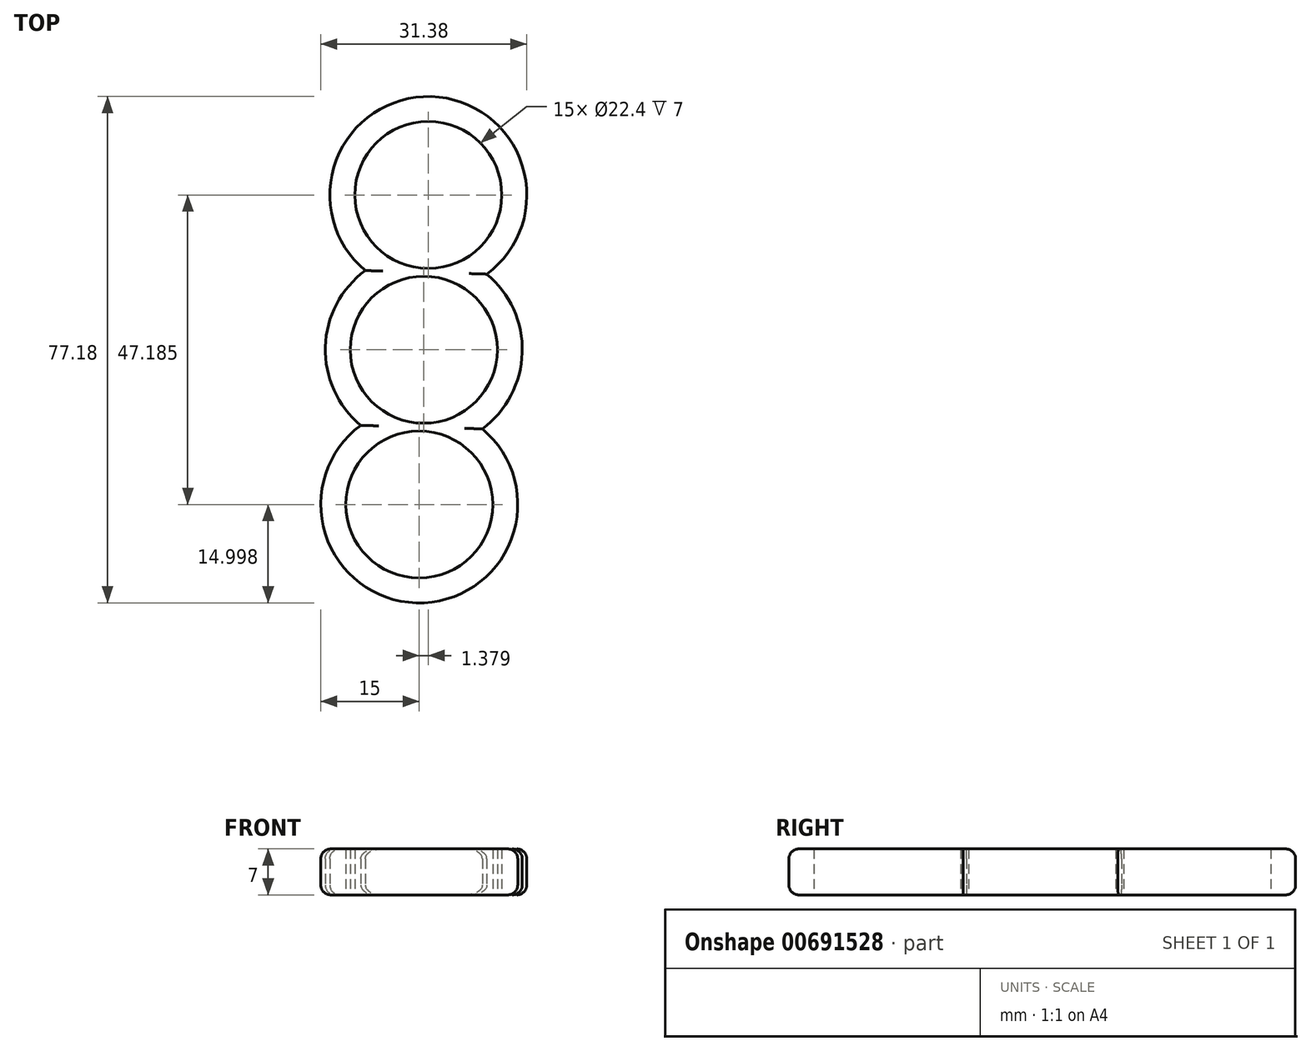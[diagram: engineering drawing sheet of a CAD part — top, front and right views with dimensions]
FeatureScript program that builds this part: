
annotation { "Feature Type Name" : "Feature", "Feature Type Description" : "" }
export const myFeature = defineFeature(function(context is Context, id is Id, definition is map)
    precondition{}
    {
        {
            var Q0;
            Q0=qCreatedBy(makeId("Top.planeOp"),FACE);
            var sketch = newSketch(context, id + "F0", { "sketchPlane" : qUnion([Q0])});
            skCircle(sketch, "E0", {"center": v(0, 0) * mm, "radius": 11.2 * mm});
            skCircle(sketch, "E1.1.0", {"center": v(-0.69, -23.6) * mm, "radius": 11.2 * mm});
            skPoint(sketch, "E1.center", {"position": v(-0.34, 1.61) * mm});
            skCircle(sketch, "E2.1.0", {"center": v(0.69, 23.6) * mm, "radius": 11.2 * mm});
            skCircle(sketch, "E3", {"center": v(-0.69, -23.6) * mm, "radius": 15 * mm});
            skCircle(sketch, "E4", {"center": v(0, 0) * mm, "radius": 15 * mm});
            skCircle(sketch, "E5", {"center": v(0.69, 23.6) * mm, "radius": 15 * mm});
            skSolve(sketch);
        }
        {
            var Q0;
            Q0=qSketchRegion(id+"F0",true);
            extrude(context, id + "F1", {"entities" : qUnion([Q0]), "depth" : 7 * mm, "offsetDistance" : 25 * mm});
        }
        {
            var Q0;
            Q0=makeQuery(id+"F1.opExtrude","CAP_EDGE",EDGE,{"disambiguationData":[OSD([sQuery(id+"F0.wireOp",EDGE,"KVhzaLa0-SQdz-q6Oe-w92h-Agfz15YDrdAH")])],"isStart":false});
            var Q1;
            Q1=makeQuery(id+"F1.opExtrude","CAP_EDGE",EDGE,{"disambiguationData":[OSD([sQuery(id+"F0.wireOp",EDGE,"ff2df07f-f202-44d3-8f0e-1026d9d6524d.2.1")])],"isStart":false});
            var Q2;
            Q2=makeQuery(id+"F1.opExtrude","CAP_EDGE",EDGE,{"disambiguationData":[OSD([sQuery(id+"F0.wireOp",EDGE,"ff2df07f-f202-44d3-8f0e-1026d9d6524d.1.1")])],"isStart":false});
            var Q3;
            Q3=makeQuery(id+"F1.opExtrude","CAP_EDGE",EDGE,{"disambiguationData":[OSD([sQuery(id+"F0.wireOp",EDGE,"E3TO4OPZ-r4YO-zi4T-4Kzq-n9bXmHvUswec")])],"isStart":false});
            var Q4;
            Q4=makeQuery(id+"F1.opExtrude","CAP_EDGE",EDGE,{"disambiguationData":[OSD([sQuery(id+"F0.wireOp",EDGE,"ff2df07f-f202-44d3-8f0e-1026d9d6524d.2.1")])],"isStart":true});
            var Q5;
            Q5=makeQuery(id+"F1.opExtrude","CAP_EDGE",EDGE,{"disambiguationData":[OSD([sQuery(id+"F0.wireOp",EDGE,"b95ef4d3-2bef-4a45-8702-1981668bb12b.1.0")])],"isStart":true});
            var Q6;
            Q6=makeQuery(id+"F1.opExtrude","CAP_EDGE",EDGE,{"disambiguationData":[OSD([sQuery(id+"F0.wireOp",EDGE,"E3TO4OPZ-r4YO-zi4T-4Kzq-n9bXmHvUswec")])],"isStart":true});
            var Q7;
            Q7=makeQuery(id+"F1.opExtrude","CAP_EDGE",EDGE,{"disambiguationData":[OSD([sQuery(id+"F0.wireOp",EDGE,"ff2df07f-f202-44d3-8f0e-1026d9d6524d.1.1")])],"isStart":true});
            var Q8;
            Q8=makeQuery(id+"F1.opExtrude","CAP_EDGE",EDGE,{"disambiguationData":[OSD([sQuery(id+"F0.wireOp",EDGE,"HvMq5l3T-N398-ElJL-TXP7-qc9evoMqA3Qe")])],"isStart":false});
            var Q9;
            Q9=makeQuery(id+"F1.opExtrude","CAP_EDGE",EDGE,{"disambiguationData":[OSD([sQuery(id+"F0.wireOp",EDGE,"6a3b17aa-de62-40af-a578-fda0c71b9185")])],"isStart":false});
            var Q10;
            Q10=makeQuery(id+"F1.opExtrude","CAP_EDGE",EDGE,{"disambiguationData":[OSD([sQuery(id+"F0.wireOp",EDGE,"HvMq5l3T-N398-ElJL-TXP7-qc9evoMqA3Qe")])],"isStart":true});
            var Q11;
            Q11=makeQuery(id+"F1.opExtrude","CAP_EDGE",EDGE,{"disambiguationData":[OSD([sQuery(id+"F0.wireOp",EDGE,"6a3b17aa-de62-40af-a578-fda0c71b9185")])],"isStart":true});
            var Q12;
            {var subQ0=sQuery(id+"F0.wireOp",EDGE,"e1ec5250-1445-4ff0-901a-2fadd4f62a60");Q12=makeQuery(id+"F1.opExtrude","CAP_EDGE",EDGE,{"disambiguationData":[OSD([subQ0]),TDD([makeQuery(id+"F0.imprint","IMPRINT",EDGE,{"disambiguationData":[TD([[makeQuery(id+"F0.imprint","INTERSECT",VERTEX,{"disambiguationData":[OD(0.0)],"derivedFrom":[sQuery(id+"F0.wireOp",EDGE,"HvMq5l3T-N398-ElJL-TXP7-qc9evoMqA3Qe"),subQ0]}),-1.0]])],"derivedFrom":subQ0})])],"isStart":false});}
            var Q13;
            {var subQ0=sQuery(id+"F0.wireOp",EDGE,"e1ec5250-1445-4ff0-901a-2fadd4f62a60");Q13=makeQuery(id+"F1.opExtrude","CAP_EDGE",EDGE,{"disambiguationData":[OSD([subQ0]),TDD([makeQuery(id+"F0.imprint","IMPRINT",EDGE,{"disambiguationData":[TD([[makeQuery(id+"F0.imprint","INTERSECT",VERTEX,{"disambiguationData":[OD(1.0)],"derivedFrom":[sQuery(id+"F0.wireOp",EDGE,"HvMq5l3T-N398-ElJL-TXP7-qc9evoMqA3Qe"),subQ0]}),1.0]])],"derivedFrom":subQ0})])],"isStart":false});}
            var Q14;
            {var subQ0=sQuery(id+"F0.wireOp",EDGE,"e1ec5250-1445-4ff0-901a-2fadd4f62a60");Q14=makeQuery(id+"F1.opExtrude","CAP_EDGE",EDGE,{"disambiguationData":[OSD([subQ0]),TDD([makeQuery(id+"F0.imprint","IMPRINT",EDGE,{"disambiguationData":[TD([[makeQuery(id+"F0.imprint","INTERSECT",VERTEX,{"disambiguationData":[OD(0.0)],"derivedFrom":[sQuery(id+"F0.wireOp",EDGE,"HvMq5l3T-N398-ElJL-TXP7-qc9evoMqA3Qe"),subQ0]}),-1.0]])],"derivedFrom":subQ0})])],"isStart":true});}
            var Q15;
            {var subQ0=sQuery(id+"F0.wireOp",EDGE,"e1ec5250-1445-4ff0-901a-2fadd4f62a60");Q15=makeQuery(id+"F1.opExtrude","CAP_EDGE",EDGE,{"disambiguationData":[OSD([subQ0]),TDD([makeQuery(id+"F0.imprint","IMPRINT",EDGE,{"disambiguationData":[TD([[makeQuery(id+"F0.imprint","INTERSECT",VERTEX,{"disambiguationData":[OD(1.0)],"derivedFrom":[sQuery(id+"F0.wireOp",EDGE,"HvMq5l3T-N398-ElJL-TXP7-qc9evoMqA3Qe"),subQ0]}),1.0]])],"derivedFrom":subQ0})])],"isStart":true});}
            var Q16;
            Q16=makeQuery(id+"F1.opExtrude","CAP_EDGE",EDGE,{"disambiguationData":[OSD([sQuery(id+"F0.wireOp",EDGE,"E3")])],"isStart":true});
            var Q17;
            {var subQ0=sQuery(id+"F0.wireOp",EDGE,"E4");Q17=makeQuery(id+"F1.opExtrude","CAP_EDGE",EDGE,{"disambiguationData":[OSD([subQ0]),TDD([makeQuery(id+"F0.imprint","IMPRINT",EDGE,{"disambiguationData":[TD([[makeQuery(id+"F0.imprint","INTERSECT",VERTEX,{"disambiguationData":[OD(1.0)],"derivedFrom":[sQuery(id+"F0.wireOp",EDGE,"E3"),subQ0]}),1.0]])],"derivedFrom":subQ0})])],"isStart":true});}
            var Q18;
            Q18=makeQuery(id+"F1.opExtrude","CAP_EDGE",EDGE,{"disambiguationData":[OSD([sQuery(id+"F0.wireOp",EDGE,"E3")])],"isStart":false});
            var Q19;
            {var subQ0=sQuery(id+"F0.wireOp",EDGE,"E4");Q19=makeQuery(id+"F1.opExtrude","CAP_EDGE",EDGE,{"disambiguationData":[OSD([subQ0]),TDD([makeQuery(id+"F0.imprint","IMPRINT",EDGE,{"disambiguationData":[TD([[makeQuery(id+"F0.imprint","INTERSECT",VERTEX,{"disambiguationData":[OD(1.0)],"derivedFrom":[sQuery(id+"F0.wireOp",EDGE,"E3"),subQ0]}),1.0]])],"derivedFrom":subQ0})])],"isStart":false});}
            var Q20;
            Q20=makeQuery(id+"F1.opExtrude","CAP_EDGE",EDGE,{"disambiguationData":[OSD([sQuery(id+"F0.wireOp",EDGE,"E5")])],"isStart":true});
            var Q21;
            Q21=makeQuery(id+"F1.opExtrude","CAP_EDGE",EDGE,{"disambiguationData":[OSD([sQuery(id+"F0.wireOp",EDGE,"E5")])],"isStart":false});
            var Q22;
            {var subQ0=sQuery(id+"F0.wireOp",EDGE,"E4");Q22=makeQuery(id+"F1.opExtrude","CAP_EDGE",EDGE,{"disambiguationData":[OSD([subQ0]),TDD([makeQuery(id+"F0.imprint","IMPRINT",EDGE,{"disambiguationData":[TD([[makeQuery(id+"F0.imprint","INTERSECT",VERTEX,{"disambiguationData":[OD(0.0)],"derivedFrom":[sQuery(id+"F0.wireOp",EDGE,"E3"),subQ0]}),-1.0]])],"derivedFrom":subQ0})])],"isStart":true});}
            var Q23;
            {var subQ0=sQuery(id+"F0.wireOp",EDGE,"E4");Q23=makeQuery(id+"F1.opExtrude","CAP_EDGE",EDGE,{"disambiguationData":[OSD([subQ0]),TDD([makeQuery(id+"F0.imprint","IMPRINT",EDGE,{"disambiguationData":[TD([[makeQuery(id+"F0.imprint","INTERSECT",VERTEX,{"disambiguationData":[OD(0.0)],"derivedFrom":[sQuery(id+"F0.wireOp",EDGE,"E3"),subQ0]}),-1.0]])],"derivedFrom":subQ0})])],"isStart":false});}
            fillet(context, id + "F2", {"entities" : qUnion([Q0, Q1, Q2, Q3, Q4, Q5, Q6, Q7, Q8, Q9, Q10, Q11, Q12, Q13, Q14, Q15, Q16, Q17, Q18, Q19, Q20, Q21, Q22, Q23]), "radius" : 1.5 * mm, "tangentPropagation" : true, "allowEdgeOverflow" : false});
        }
    });
